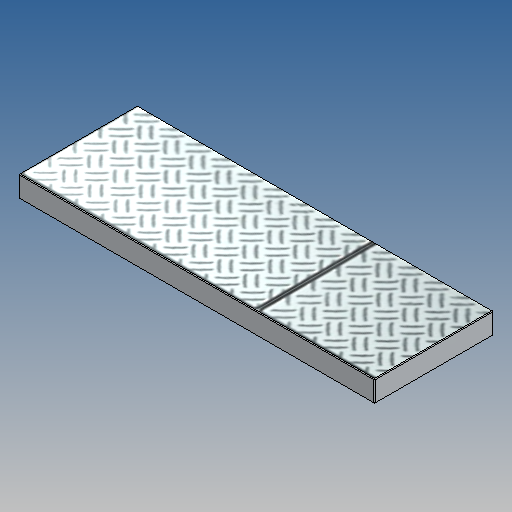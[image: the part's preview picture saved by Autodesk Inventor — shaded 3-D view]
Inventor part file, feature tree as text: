
AUTODESK INVENTOR PART (.ipt)
format: ipt  version: 2025 (Build 290162010, 162A)  size: 367,104 bytes
history: native  units: in
note: dims shown in document units (in); Inventor stores cm internally (conversion verified against a paired STEP export)
features: other x6, extrude x3, sketch x2, fillet x1
ambient origin geometry x8: Origin, YZ Plane, XZ Plane, XY Plane, X Axis, Y Axis, Z Axis, Center Point
bodies: Solid1 (feature_tree)
feature tree (12):
  sketch  "Sketch2"  dims[d0=0.6299in d1=1.8898in]
  extrude  "Extrusion1"  Depth=1.8898in
  extrude  "Extrusion2"  Depth=0.0157in
  extrude  "Extrusion3"  Depth=0.0039in
  fillet  "Fillet1"  Radius=0.252in
  other  "Work Axis1"
  other  "Work Axis2"
  other  "Work Axis3"
  other  "Work Axis4"
  other  "Aufkleber1"
  sketch  "Skizze3"  dims[d2=0.0157in d3=0.0157in d4=0.189in d5=0.252in d6=0.315in d7=0.063in d8=0.063in d9=0.126in d10=0.0in d11=0.0157in d12=0.0in d13=0.063in d14=0.0in d15=0.189in d16=0.0039in d17=0.0in d18=0.0in d19=0.0in d20=0.0in d21=0.0in d22=0.0in d23=0.0in d43=0.0039in d44=0.0236in d45=0.0354in]
  other  "Bild4"
